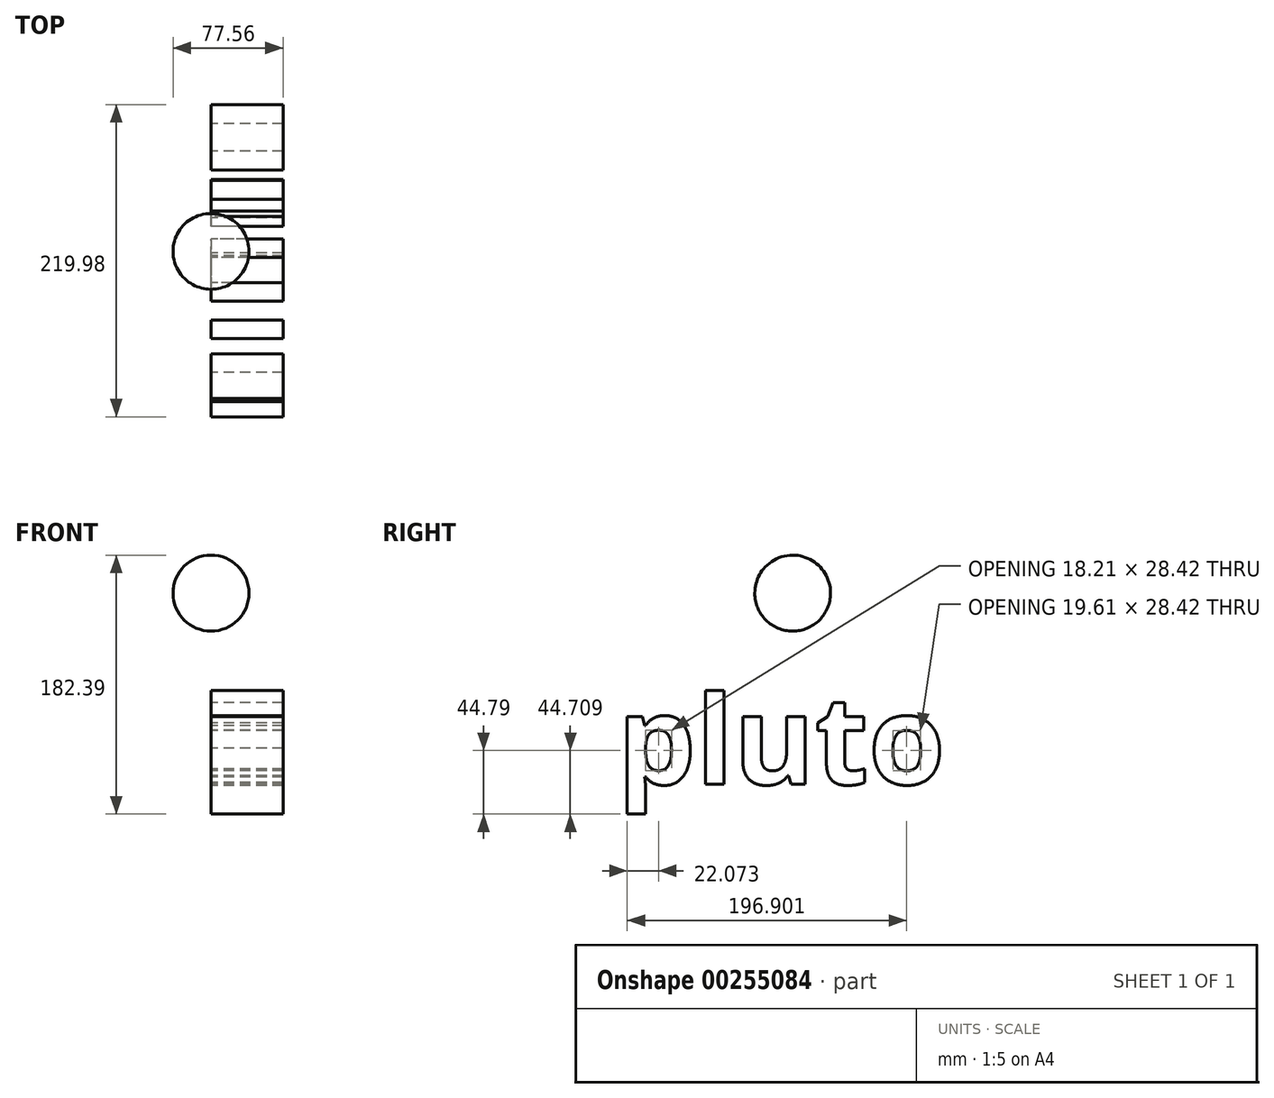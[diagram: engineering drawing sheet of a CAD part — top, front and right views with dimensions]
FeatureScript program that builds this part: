
annotation { "Feature Type Name" : "Feature", "Feature Type Description" : "" }
export const myFeature = defineFeature(function(context is Context, id is Id, definition is map)
    precondition{}
    {
        {
            var Q0;
            Q0=qCreatedBy(makeId("Top.planeOp"),FACE);
            var sketch = newSketch(context, id + "F0", { "sketchPlane" : qUnion([Q0])});
            skLineSegment(sketch, "E0", {"start": v(0, 0) * mm, "end": v(0, 53.32) * mm});
            skArc(sketch, "E1", {"start": v(0, 0) * mm, "mid": v(26.76, 26.66) * mm, "end": v(0, 53.32) * mm});
            skSolve(sketch);
        }
        {
            var Q0;
            Q0 = qSketchRegion(id + "F0", true);
            var Q1;
            Q1=sQuery(id+"F0.wireOp",EDGE,"E0");
            revolve(context, id + "F1", {"entities" : qUnion([Q0]), "axis" : qUnion([Q1]), "revolveType" : RevolveType.FULL});
        }
        {
            var Q0;
            Q0=qCreatedBy(makeId("Right.planeOp"),FACE);
            var sketch = newSketch(context, id + "F2", { "sketchPlane" : qUnion([Q0])});
            skText(sketch, "E2", { "text": "pluto", "fontName": "OpenSans-Bold.ttf"});
            const initialGuessF2  = {"E2": [-0.09668, -0.1347, 1, 0, 0.06272]};
            skSetInitialGuess(sketch, initialGuessF2);
            skSolve(sketch);
        }
        {
            var Q0;
            Q0=makeQuery(id+"F2.imprint","IMPRINT",FACE,{"disambiguationData":[TD([[makeQuery(id+"F2.imprint","IMPRINT",EDGE,{"derivedFrom":sQuery(id+"F2.wireOp",EDGE,"E2.sketch_text.stroke-44")}),-1.0]])]});
            var Q1;
            Q1=makeQuery(id+"F2.imprint","IMPRINT",FACE,{"disambiguationData":[TD([[makeQuery(id+"F2.imprint","IMPRINT",EDGE,{"derivedFrom":sQuery(id+"F2.wireOp",EDGE,"E2.sketch_text.stroke-27")}),-1.0]])]});
            var Q2;
            Q2=makeQuery(id+"F2.imprint","IMPRINT",FACE,{"disambiguationData":[TD([[makeQuery(id+"F2.imprint","IMPRINT",EDGE,{"derivedFrom":sQuery(id+"F2.wireOp",EDGE,"E2.sketch_text.stroke-23")}),-1.0]])]});
            var Q3;
            Q3=makeQuery(id+"F2.imprint","IMPRINT",FACE,{"disambiguationData":[TD([[makeQuery(id+"F2.imprint","IMPRINT",EDGE,{"derivedFrom":sQuery(id+"F2.wireOp",EDGE,"E2.sketch_text.stroke-0")}),-1.0]])]});
            var Q4;
            Q4=makeQuery(id+"F2.imprint","IMPRINT",FACE,{"disambiguationData":[TD([[makeQuery(id+"F2.imprint","IMPRINT",EDGE,{"derivedFrom":sQuery(id+"F2.wireOp",EDGE,"E2.sketch_text.stroke-62")}),-1.0]])]});
            extrude(context, id + "F3", {"entities" : qUnion([Q0, Q1, Q2, Q3, Q4]), "depth" : 50.8 * mm});
        }
    });
